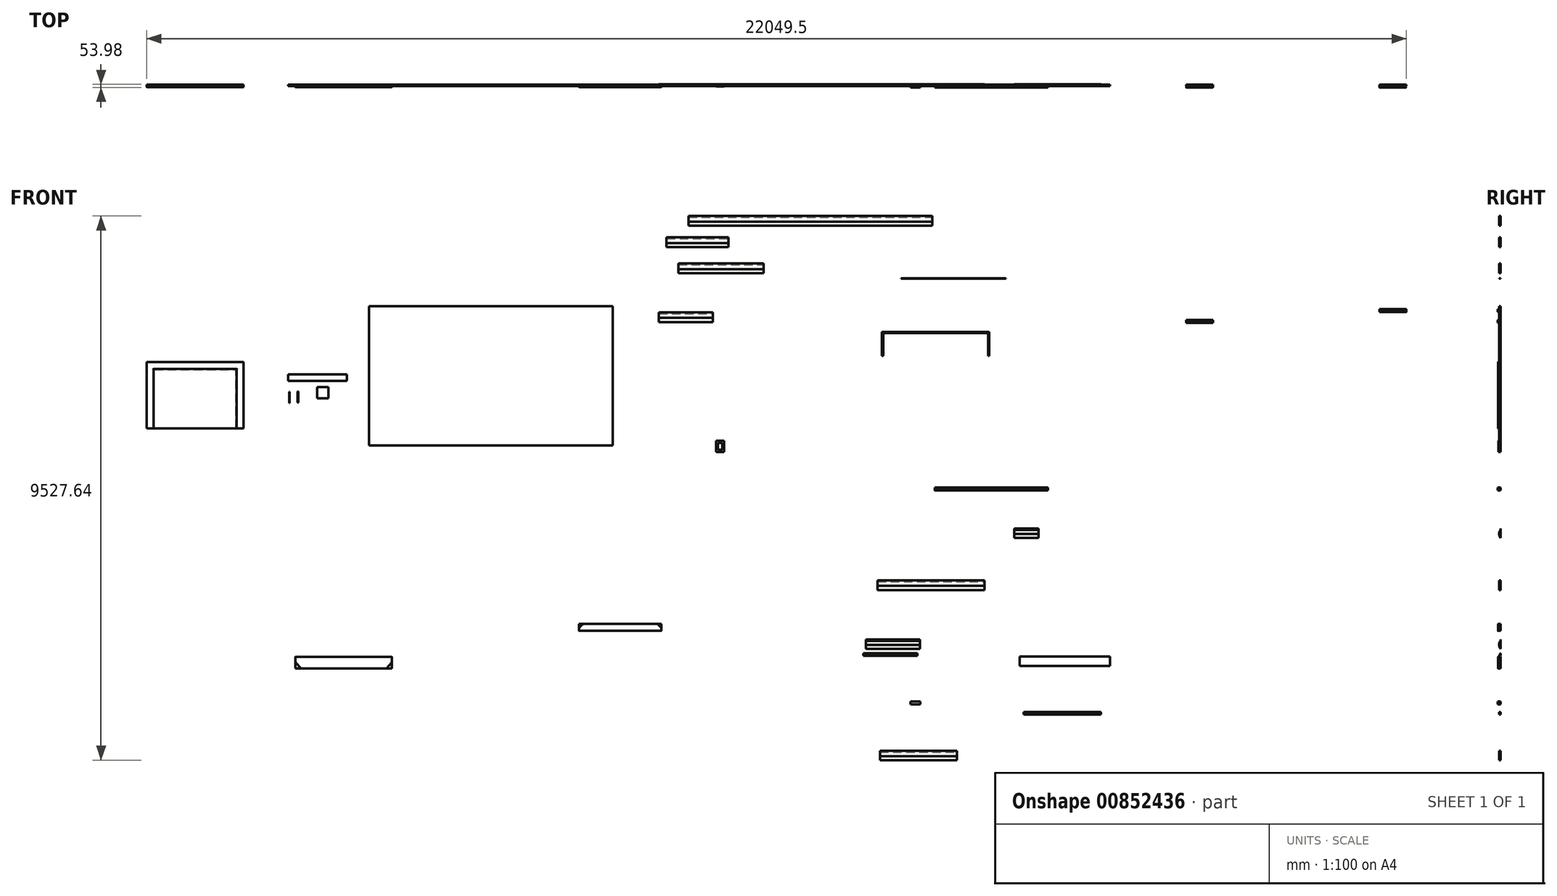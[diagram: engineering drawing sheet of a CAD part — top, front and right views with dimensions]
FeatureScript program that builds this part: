
annotation { "Feature Type Name" : "Feature", "Feature Type Description" : "" }
export const myFeature = defineFeature(function(context is Context, id is Id, definition is map)
    precondition{}
    {
        {
            var Q0;
            Q0=qCreatedBy(makeId("Front.planeOp"),FACE);
            var sketch = newSketch(context, id + "F0", { "sketchPlane" : qUnion([Q0])});
            skLineSegment(sketch, "E0.bottom", {"start": v(2133.6, -1219.2) * mm, "end": v(-2133.6, -1219.2) * mm});
            skLineSegment(sketch, "E0.top", {"start": v(2133.6, 1219.2) * mm, "end": v(-2133.6, 1219.2) * mm});
            skLineSegment(sketch, "E0.left", {"start": v(2133.6, -1219.2) * mm, "end": v(2133.6, 1219.2) * mm});
            skLineSegment(sketch, "E0.right", {"start": v(-2133.6, -1219.2) * mm, "end": v(-2133.6, 1219.2) * mm});
            skPoint(sketch, "E0.middle", {"position": v(0, 0) * mm});
            skLineSegment(sketch, "E1", {"start": v(1047.75, -1219.2) * mm, "end": v(1047.75, 274.79) * mm, "construction": true});
            skLineSegment(sketch, "E2", {"start": v(-644.53, -1219.2) * mm, "end": v(-644.53, 378.54) * mm, "construction": true});
            skLineSegment(sketch, "E3", {"start": v(-966.88, 254) * mm, "end": v(1301.85, 254) * mm, "construction": true});
            skLineSegment(sketch, "E4.bottom", {"start": v(3460.45, 2798.97) * mm, "end": v(7727.65, 2798.97) * mm});
            skLineSegment(sketch, "E4.top", {"start": v(3460.45, 2627.52) * mm, "end": v(7727.65, 2627.52) * mm});
            skLineSegment(sketch, "E4.left", {"start": v(3460.45, 2798.97) * mm, "end": v(3460.45, 2627.52) * mm});
            skLineSegment(sketch, "E4.right", {"start": v(7727.65, 2798.97) * mm, "end": v(7727.65, 2627.52) * mm});
            skLineSegment(sketch, "E5", {"start": v(3460.45, 2773.57) * mm, "end": v(7727.65, 2773.57) * mm});
            skLineSegment(sketch, "E6.bottom", {"start": v(4161.2, 2251.66) * mm, "end": v(3075.35, 2251.66) * mm});
            skLineSegment(sketch, "E6.top", {"start": v(4161.2, 2423.11) * mm, "end": v(3075.35, 2423.11) * mm});
            skLineSegment(sketch, "E6.left", {"start": v(4161.2, 2251.66) * mm, "end": v(4161.2, 2423.11) * mm});
            skLineSegment(sketch, "E6.right", {"start": v(3075.35, 2251.66) * mm, "end": v(3075.35, 2423.11) * mm});
            skPoint(sketch, "E6.middle", {"position": v(3618.27, 2337.39) * mm});
            skLineSegment(sketch, "E7.bottom", {"start": v(4772.4, 1795.08) * mm, "end": v(3283.32, 1795.08) * mm});
            skLineSegment(sketch, "E7.top", {"start": v(4772.4, 1966.53) * mm, "end": v(3283.32, 1966.53) * mm});
            skLineSegment(sketch, "E7.left", {"start": v(4772.4, 1795.08) * mm, "end": v(4772.4, 1966.53) * mm});
            skLineSegment(sketch, "E7.right", {"start": v(3283.32, 1795.08) * mm, "end": v(3283.32, 1966.53) * mm});
            skPoint(sketch, "E7.middle", {"position": v(4027.86, 1880.8) * mm});
            skLineSegment(sketch, "E8", {"start": v(3075.35, 2397.71) * mm, "end": v(4161.2, 2397.71) * mm});
            skLineSegment(sketch, "E9", {"start": v(3283.32, 1941.13) * mm, "end": v(4772.4, 1941.13) * mm});
            skLineSegment(sketch, "E10.bottom", {"start": v(4082.73, -1332.54) * mm, "end": v(3943.03, -1332.54) * mm});
            skLineSegment(sketch, "E10.top", {"start": v(4082.73, -1135.69) * mm, "end": v(3943.03, -1135.69) * mm});
            skLineSegment(sketch, "E10.left", {"start": v(4082.73, -1332.54) * mm, "end": v(4082.73, -1135.69) * mm});
            skLineSegment(sketch, "E10.right", {"start": v(3943.03, -1332.54) * mm, "end": v(3943.03, -1135.69) * mm});
            skPoint(sketch, "E10.middle", {"position": v(4012.88, -1234.11) * mm});
            skLineSegment(sketch, "E11.bottom", {"start": v(4051.44, -1295.6) * mm, "end": v(3974.33, -1295.6) * mm});
            skLineSegment(sketch, "E11.top", {"start": v(4051.44, -1172.61) * mm, "end": v(3974.33, -1172.61) * mm});
            skLineSegment(sketch, "E11.left", {"start": v(4051.44, -1295.6) * mm, "end": v(4051.44, -1172.61) * mm});
            skLineSegment(sketch, "E11.right", {"start": v(3974.33, -1295.6) * mm, "end": v(3974.33, -1172.61) * mm});
            skLineSegment(sketch, "E12.bottom", {"start": v(3886, 940.69) * mm, "end": v(2939.84, 940.69) * mm});
            skLineSegment(sketch, "E12.top", {"start": v(3886, 1112.14) * mm, "end": v(2939.84, 1112.14) * mm});
            skLineSegment(sketch, "E12.left", {"start": v(3886, 940.69) * mm, "end": v(3886, 1112.14) * mm});
            skLineSegment(sketch, "E12.right", {"start": v(2939.84, 940.69) * mm, "end": v(2939.84, 1112.14) * mm});
            skPoint(sketch, "E12.middle", {"position": v(3412.92, 1026.41) * mm});
            skLineSegment(sketch, "E13", {"start": v(2939.84, 1086.74) * mm, "end": v(3886, 1086.74) * mm});
            skLineSegment(sketch, "E14.bottom", {"start": v(-1731.12, -5127.06) * mm, "end": v(-3423.4, -5127.06) * mm});
            skLineSegment(sketch, "E14.top", {"start": v(-1731.12, -4923.86) * mm, "end": v(-3423.4, -4923.86) * mm});
            skLineSegment(sketch, "E14.left", {"start": v(-1731.12, -5127.06) * mm, "end": v(-1731.12, -4923.86) * mm});
            skLineSegment(sketch, "E14.right", {"start": v(-3423.4, -5127.06) * mm, "end": v(-3423.4, -4923.86) * mm});
            skPoint(sketch, "E14.middle", {"position": v(-2577.25, -5025.46) * mm});
            skLineSegment(sketch, "E15", {"start": v(-3423.4, -5012.76) * mm, "end": v(-3321.8, -5127.06) * mm});
            skLineSegment(sketch, "E16", {"start": v(-1832.72, -5127.06) * mm, "end": v(-1731.12, -5012.76) * mm});
            skLineSegment(sketch, "E17.bottom", {"start": v(2982.98, -4465.71) * mm, "end": v(1544.7, -4465.71) * mm});
            skLineSegment(sketch, "E17.top", {"start": v(2982.98, -4345.06) * mm, "end": v(1544.7, -4345.06) * mm});
            skLineSegment(sketch, "E17.left", {"start": v(2982.98, -4465.71) * mm, "end": v(2982.98, -4345.06) * mm});
            skLineSegment(sketch, "E17.right", {"start": v(1544.7, -4465.71) * mm, "end": v(1544.7, -4345.06) * mm});
            skPoint(sketch, "E17.middle", {"position": v(2263.85, -4405.39) * mm});
            skLineSegment(sketch, "E18.bottom", {"start": v(-4331.9, -920.82) * mm, "end": v(-6024.17, -920.82) * mm});
            skLineSegment(sketch, "E18.top", {"start": v(-4331.9, 238.05) * mm, "end": v(-6024.17, 238.05) * mm});
            skLineSegment(sketch, "E18.left", {"start": v(-4331.9, -920.82) * mm, "end": v(-4331.9, 238.05) * mm});
            skLineSegment(sketch, "E18.right", {"start": v(-6024.17, -920.82) * mm, "end": v(-6024.17, 238.05) * mm});
            skLineSegment(sketch, "E19.bottom", {"start": v(-4452.55, -920.82) * mm, "end": v(-5903.52, -920.82) * mm});
            skLineSegment(sketch, "E19.top", {"start": v(-4452.55, 117.4) * mm, "end": v(-5903.52, 117.4) * mm});
            skLineSegment(sketch, "E19.left", {"start": v(-4452.55, -920.82) * mm, "end": v(-4452.55, 117.4) * mm});
            skLineSegment(sketch, "E19.right", {"start": v(-5903.52, -920.82) * mm, "end": v(-5903.52, 117.4) * mm});
            skLineSegment(sketch, "E20.bottom", {"start": v(-5890.82, -920.82) * mm, "end": v(-4465.25, -920.82) * mm});
            skLineSegment(sketch, "E20.top", {"start": v(-5890.82, 107.88) * mm, "end": v(-4465.25, 107.88) * mm});
            skLineSegment(sketch, "E20.left", {"start": v(-5890.82, -920.82) * mm, "end": v(-5890.82, 107.88) * mm});
            skLineSegment(sketch, "E20.right", {"start": v(-4465.25, -920.82) * mm, "end": v(-4465.25, 107.88) * mm});
            skLineSegment(sketch, "E21.bottom", {"start": v(-3522.66, -473.47) * mm, "end": v(-3530.6, -473.47) * mm});
            skLineSegment(sketch, "E21.top", {"start": v(-3522.66, -276.62) * mm, "end": v(-3530.6, -276.62) * mm});
            skLineSegment(sketch, "E21.left", {"start": v(-3522.66, -473.47) * mm, "end": v(-3522.66, -276.62) * mm});
            skLineSegment(sketch, "E21.right", {"start": v(-3530.6, -473.47) * mm, "end": v(-3530.6, -276.62) * mm});
            skPoint(sketch, "E21.middle", {"position": v(-3526.63, -375.05) * mm});
            skLineSegment(sketch, "E22.bottom", {"start": v(-2844.05, -391.52) * mm, "end": v(-3040.9, -391.52) * mm});
            skLineSegment(sketch, "E22.top", {"start": v(-2844.05, -194.67) * mm, "end": v(-3040.9, -194.67) * mm});
            skLineSegment(sketch, "E22.left", {"start": v(-2844.05, -391.52) * mm, "end": v(-2844.05, -194.67) * mm});
            skLineSegment(sketch, "E22.right", {"start": v(-3040.9, -391.52) * mm, "end": v(-3040.9, -194.67) * mm});
            skPoint(sketch, "E22.middle", {"position": v(-2942.48, -293.1) * mm});
            skLineSegment(sketch, "E23.bottom", {"start": v(-3373.18, -472.42) * mm, "end": v(-3385.88, -472.42) * mm});
            skLineSegment(sketch, "E23.top", {"start": v(-3373.18, -275.57) * mm, "end": v(-3385.88, -275.57) * mm});
            skLineSegment(sketch, "E23.left", {"start": v(-3373.18, -472.42) * mm, "end": v(-3373.18, -275.57) * mm});
            skLineSegment(sketch, "E23.right", {"start": v(-3385.88, -472.42) * mm, "end": v(-3385.88, -275.57) * mm});
            skPoint(sketch, "E23.middle", {"position": v(-3379.53, -374) * mm});
            skLineSegment(sketch, "E24.bottom", {"start": v(9756.5, -2005.6) * mm, "end": v(7775.3, -2005.6) * mm});
            skLineSegment(sketch, "E24.top", {"start": v(9756.5, -1954.8) * mm, "end": v(7775.3, -1954.8) * mm});
            skLineSegment(sketch, "E24.left", {"start": v(9756.5, -2005.6) * mm, "end": v(9756.5, -1954.8) * mm});
            skLineSegment(sketch, "E24.right", {"start": v(7775.3, -2005.6) * mm, "end": v(7775.3, -1954.8) * mm});
            skPoint(sketch, "E24.middle", {"position": v(8765.9, -1980.2) * mm});
            skLineSegment(sketch, "E25.bottom", {"start": v(12640.94, 979.02) * mm, "end": v(12171.04, 979.02) * mm});
            skLineSegment(sketch, "E25.top", {"start": v(12640.94, 928.22) * mm, "end": v(12171.04, 928.22) * mm});
            skLineSegment(sketch, "E25.left", {"start": v(12640.94, 979.02) * mm, "end": v(12640.94, 928.22) * mm});
            skLineSegment(sketch, "E25.right", {"start": v(12171.04, 979.02) * mm, "end": v(12171.04, 928.22) * mm});
            skPoint(sketch, "E25.middle", {"position": v(12405.99, 953.62) * mm});
            skLineSegment(sketch, "E26.bottom", {"start": v(16025.35, 1169.27) * mm, "end": v(15555.45, 1169.27) * mm});
            skLineSegment(sketch, "E26.top", {"start": v(16025.35, 1118.47) * mm, "end": v(15555.45, 1118.47) * mm});
            skLineSegment(sketch, "E26.left", {"start": v(16025.35, 1169.27) * mm, "end": v(16025.35, 1118.47) * mm});
            skLineSegment(sketch, "E26.right", {"start": v(15555.45, 1169.27) * mm, "end": v(15555.45, 1118.47) * mm});
            skPoint(sketch, "E26.middle", {"position": v(15790.4, 1143.87) * mm});
            skLineSegment(sketch, "E27.bottom", {"start": v(8727.97, 351.1) * mm, "end": v(8705.74, 351.1) * mm});
            skLineSegment(sketch, "E27.top", {"start": v(8727.97, 770.2) * mm, "end": v(6848.37, 770.2) * mm});
            skLineSegment(sketch, "E27.left", {"start": v(8727.97, 351.1) * mm, "end": v(8727.97, 770.2) * mm});
            skLineSegment(sketch, "E27.right", {"start": v(6848.37, 351.1) * mm, "end": v(6848.37, 770.2) * mm});
            skPoint(sketch, "E27.middle", {"position": v(7788.17, 560.64) * mm});
            skLineSegment(sketch, "E28.top", {"start": v(6870.6, 751.46) * mm, "end": v(8705.74, 751.46) * mm});
            skLineSegment(sketch, "E28.left", {"start": v(6870.6, 351.1) * mm, "end": v(6870.6, 751.46) * mm});
            skLineSegment(sketch, "E28.right", {"start": v(8705.74, 351.1) * mm, "end": v(8705.74, 751.46) * mm});
            skLineSegment(sketch, "E29.trimOffspring", {"start": v(6870.6, 351.1) * mm, "end": v(6848.37, 351.1) * mm});
            skLineSegment(sketch, "E30.bottom", {"start": v(-2520.18, -86.53) * mm, "end": v(-3552.06, -86.53) * mm});
            skLineSegment(sketch, "E30.top", {"start": v(-2520.18, 27.77) * mm, "end": v(-3552.06, 27.77) * mm});
            skLineSegment(sketch, "E30.left", {"start": v(-2520.18, -86.53) * mm, "end": v(-2520.18, 27.77) * mm});
            skLineSegment(sketch, "E30.right", {"start": v(-3552.06, -86.53) * mm, "end": v(-3552.06, 27.77) * mm});
            skPoint(sketch, "E30.middle", {"position": v(-3036.12, -29.38) * mm});
            skLineSegment(sketch, "E31.bottom", {"start": v(9016.83, 1702.28) * mm, "end": v(7181.68, 1702.28) * mm});
            skLineSegment(sketch, "E31.top", {"start": v(9016.83, 1710.22) * mm, "end": v(7181.68, 1710.22) * mm});
            skLineSegment(sketch, "E31.left", {"start": v(9016.83, 1702.28) * mm, "end": v(9016.83, 1710.22) * mm});
            skLineSegment(sketch, "E31.right", {"start": v(7181.68, 1702.28) * mm, "end": v(7181.68, 1710.22) * mm});
            skPoint(sketch, "E31.middle", {"position": v(8099.26, 1706.25) * mm});
            skLineSegment(sketch, "E32.bottom", {"start": v(6770.2, -3752.52) * mm, "end": v(8639.64, -3752.52) * mm});
            skLineSegment(sketch, "E32.top", {"start": v(6770.2, -3581.07) * mm, "end": v(8639.64, -3581.07) * mm});
            skLineSegment(sketch, "E32.left", {"start": v(6770.2, -3752.52) * mm, "end": v(6770.2, -3581.07) * mm});
            skLineSegment(sketch, "E32.right", {"start": v(8639.64, -3752.52) * mm, "end": v(8639.64, -3581.07) * mm});
            skLineSegment(sketch, "E33.bottom", {"start": v(7344.23, -5752.08) * mm, "end": v(7515.68, -5752.08) * mm});
            skLineSegment(sketch, "E33.top", {"start": v(7344.23, -5701.28) * mm, "end": v(7515.68, -5701.28) * mm});
            skLineSegment(sketch, "E33.left", {"start": v(7344.23, -5752.08) * mm, "end": v(7344.23, -5701.28) * mm});
            skLineSegment(sketch, "E33.right", {"start": v(7515.68, -5752.08) * mm, "end": v(7515.68, -5701.28) * mm});
            skLineSegment(sketch, "E34.bottom", {"start": v(6811, -6728.67) * mm, "end": v(8160.37, -6728.67) * mm});
            skLineSegment(sketch, "E34.top", {"start": v(6811, -6563.57) * mm, "end": v(8160.37, -6563.57) * mm});
            skLineSegment(sketch, "E34.left", {"start": v(6811, -6728.67) * mm, "end": v(6811, -6563.57) * mm});
            skLineSegment(sketch, "E34.right", {"start": v(8160.37, -6728.67) * mm, "end": v(8160.37, -6563.57) * mm});
            skLineSegment(sketch, "E35", {"start": v(6770.2, -3606.47) * mm, "end": v(8639.64, -3606.47) * mm});
            skLineSegment(sketch, "E36", {"start": v(6811, -6588.97) * mm, "end": v(8160.37, -6588.97) * mm});
            skLineSegment(sketch, "E37.bottom", {"start": v(6564.1, -4778.8) * mm, "end": v(7510.25, -4778.8) * mm});
            skLineSegment(sketch, "E37.top", {"start": v(6564.1, -4613.7) * mm, "end": v(7510.25, -4613.7) * mm});
            skLineSegment(sketch, "E37.left", {"start": v(6564.1, -4778.8) * mm, "end": v(6564.1, -4613.7) * mm});
            skLineSegment(sketch, "E37.right", {"start": v(7510.25, -4778.8) * mm, "end": v(7510.25, -4613.7) * mm});
            skLineSegment(sketch, "E38.bottom", {"start": v(9256.06, -5080.82) * mm, "end": v(10837.31, -5080.82) * mm});
            skLineSegment(sketch, "E38.top", {"start": v(9256.06, -4915.72) * mm, "end": v(10837.31, -4915.72) * mm});
            skLineSegment(sketch, "E38.left", {"start": v(9256.06, -5080.82) * mm, "end": v(9256.06, -4915.72) * mm});
            skLineSegment(sketch, "E38.right", {"start": v(10837.31, -5080.82) * mm, "end": v(10837.31, -4915.72) * mm});
            skLineSegment(sketch, "E39.bottom", {"start": v(9329.57, -5932.4) * mm, "end": v(10678.95, -5932.4) * mm});
            skLineSegment(sketch, "E39.top", {"start": v(9329.57, -5887.95) * mm, "end": v(10678.95, -5887.95) * mm});
            skLineSegment(sketch, "E39.left", {"start": v(9329.57, -5932.4) * mm, "end": v(9329.57, -5887.95) * mm});
            skLineSegment(sketch, "E39.right", {"start": v(10678.95, -5932.4) * mm, "end": v(10678.95, -5887.95) * mm});
            skLineSegment(sketch, "E40", {"start": v(6564.1, -4639.1) * mm, "end": v(7510.25, -4639.1) * mm});
            skLineSegment(sketch, "E41.bottom", {"start": v(6523.58, -4857.86) * mm, "end": v(7469.73, -4857.86) * mm});
            skLineSegment(sketch, "E41.top", {"start": v(6523.58, -4902.3) * mm, "end": v(7469.73, -4902.3) * mm});
            skLineSegment(sketch, "E41.left", {"start": v(6523.58, -4857.86) * mm, "end": v(6523.58, -4902.3) * mm});
            skLineSegment(sketch, "E41.right", {"start": v(7469.73, -4857.86) * mm, "end": v(7469.73, -4902.3) * mm});
            skLineSegment(sketch, "E42.bottom", {"start": v(9586.54, -2837.34) * mm, "end": v(9161.1, -2837.34) * mm});
            skLineSegment(sketch, "E42.top", {"start": v(9586.54, -2672.24) * mm, "end": v(9161.1, -2672.24) * mm});
            skLineSegment(sketch, "E42.left", {"start": v(9586.54, -2837.34) * mm, "end": v(9586.54, -2672.24) * mm});
            skLineSegment(sketch, "E42.right", {"start": v(9161.1, -2837.34) * mm, "end": v(9161.1, -2672.24) * mm});
            skPoint(sketch, "E42.middle", {"position": v(9373.82, -2754.79) * mm});
            skLineSegment(sketch, "E43", {"start": v(9161.1, -2697.64) * mm, "end": v(9586.54, -2697.64) * mm});
            skSolve(sketch);
        }
        {
            var Q0;
            {var subQ0=sQuery(id+"F0.wireOp",EDGE,"E7.bottom");Q0=makeQuery(id+"F0.imprint","IMPRINT",FACE,{"disambiguationData":[TD([[makeQuery(id+"F0.imprint","IMPRINT",EDGE,{"derivedFrom":subQ0}),-1.0]])]});}
            var Q1;
            {var subQ0=sQuery(id+"F0.wireOp",EDGE,"E4.top");Q1=makeQuery(id+"F0.imprint","IMPRINT",FACE,{"disambiguationData":[TD([[makeQuery(id+"F0.imprint","IMPRINT",EDGE,{"derivedFrom":subQ0}),1.0]])]});}
            var Q2;
            {var subQ0=sQuery(id+"F0.wireOp",EDGE,"E6.bottom");Q2=makeQuery(id+"F0.imprint","IMPRINT",FACE,{"disambiguationData":[TD([[makeQuery(id+"F0.imprint","IMPRINT",EDGE,{"derivedFrom":subQ0}),-1.0]])]});}
            var Q3;
            {var subQ0=sQuery(id+"F0.wireOp",EDGE,"E12.bottom");Q3=makeQuery(id+"F0.imprint","IMPRINT",FACE,{"disambiguationData":[TD([[makeQuery(id+"F0.imprint","IMPRINT",EDGE,{"derivedFrom":subQ0}),-1.0]])]});}
            extrude(context, id + "F1", {"entities" : qUnion([Q0, Q1, Q2, Q3]), "depth" : 25.4 * mm, "offsetDistance" : 25.4 * mm});
        }
        {
            var Q0;
            Q0=makeQuery(id+"F1.opExtrude","CAP_EDGE",EDGE,{"disambiguationData":[OSD([sQuery(id+"F0.wireOp",EDGE,"E4.top")])],"isStart":false});
            var Q1;
            Q1=makeQuery(id+"F1.opExtrude","CAP_EDGE",EDGE,{"disambiguationData":[OSD([sQuery(id+"F0.wireOp",EDGE,"E5")])],"isStart":false});
            var Q2;
            Q2=makeQuery(id+"F1.opExtrude","CAP_EDGE",EDGE,{"disambiguationData":[OSD([sQuery(id+"F0.wireOp",EDGE,"E6.bottom")])],"isStart":false});
            var Q3;
            Q3=makeQuery(id+"F1.opExtrude","CAP_EDGE",EDGE,{"disambiguationData":[OSD([sQuery(id+"F0.wireOp",EDGE,"E8")])],"isStart":false});
            var Q4;
            Q4=makeQuery(id+"F1.opExtrude","CAP_EDGE",EDGE,{"disambiguationData":[OSD([sQuery(id+"F0.wireOp",EDGE,"E9")])],"isStart":false});
            var Q5;
            Q5=makeQuery(id+"F1.opExtrude","CAP_EDGE",EDGE,{"disambiguationData":[OSD([sQuery(id+"F0.wireOp",EDGE,"E7.bottom")])],"isStart":false});
            var Q6;
            Q6=makeQuery(id+"F1.opExtrude","CAP_EDGE",EDGE,{"disambiguationData":[OSD([sQuery(id+"F0.wireOp",EDGE,"E13")])],"isStart":false});
            var Q7;
            Q7=makeQuery(id+"F1.opExtrude","CAP_EDGE",EDGE,{"disambiguationData":[OSD([sQuery(id+"F0.wireOp",EDGE,"E12.bottom")])],"isStart":false});
            fillet(context, id + "F2", {"entities" : qUnion([Q0, Q1, Q2, Q3, Q4, Q5, Q6, Q7]), "radius" : 127 * mm, "tangentPropagation" : true, "allowEdgeOverflow" : false});
        }
        {
            var Q0;
            {var subQ0=sQuery(id+"F0.wireOp",EDGE,"E6.bottom");Q0=makeQuery(id+"F0.imprint","IMPRINT",FACE,{"disambiguationData":[TD([[makeQuery(id+"F0.imprint","IMPRINT",EDGE,{"derivedFrom":subQ0}),-1.0]])]});}
            var Q1;
            {var subQ0=sQuery(id+"F0.wireOp",EDGE,"E6.top");Q1=makeQuery(id+"F0.imprint","IMPRINT",FACE,{"disambiguationData":[TD([[makeQuery(id+"F0.imprint","IMPRINT",EDGE,{"derivedFrom":subQ0}),1.0]])]});}
            extrude(context, id + "F3", {"entities" : qUnion([Q0, Q1]), "operationType" : NewBodyOperationType.ADD, "oppositeDirection" : true, "depth" : 3.17 * mm, "offsetDistance" : 25.4 * mm});
        }
        {
            var Q0;
            {var subQ0=sQuery(id+"F0.wireOp",EDGE,"E7.top");Q0=makeQuery(id+"F0.imprint","IMPRINT",FACE,{"disambiguationData":[TD([[makeQuery(id+"F0.imprint","IMPRINT",EDGE,{"derivedFrom":subQ0}),1.0]])]});}
            var Q1;
            {var subQ0=sQuery(id+"F0.wireOp",EDGE,"E7.bottom");Q1=makeQuery(id+"F0.imprint","IMPRINT",FACE,{"disambiguationData":[TD([[makeQuery(id+"F0.imprint","IMPRINT",EDGE,{"derivedFrom":subQ0}),-1.0]])]});}
            extrude(context, id + "F4", {"entities" : qUnion([Q0, Q1]), "operationType" : NewBodyOperationType.ADD, "oppositeDirection" : true, "depth" : 3.17 * mm, "offsetDistance" : 25.4 * mm});
        }
        {
            var Q0;
            {var subQ0=sQuery(id+"F0.wireOp",EDGE,"E4.top");Q0=makeQuery(id+"F0.imprint","IMPRINT",FACE,{"disambiguationData":[TD([[makeQuery(id+"F0.imprint","IMPRINT",EDGE,{"derivedFrom":subQ0}),1.0]])]});}
            var Q1;
            {var subQ0=sQuery(id+"F0.wireOp",EDGE,"E4.bottom");Q1=makeQuery(id+"F0.imprint","IMPRINT",FACE,{"disambiguationData":[TD([[makeQuery(id+"F0.imprint","IMPRINT",EDGE,{"derivedFrom":subQ0}),-1.0]])]});}
            extrude(context, id + "F5", {"entities" : qUnion([Q0, Q1]), "operationType" : NewBodyOperationType.ADD, "oppositeDirection" : true, "depth" : 3.17 * mm, "offsetDistance" : 25.4 * mm});
        }
        {
            var Q0;
            Q0=makeQuery(id+"F0.imprint","IMPRINT",FACE,{"disambiguationData":[TD([[makeQuery(id+"F0.imprint","IMPRINT",EDGE,{"derivedFrom":sQuery(id+"F0.wireOp",EDGE,"E10.bottom")}),-1.0]])]});
            extrude(context, id + "F6", {"entities" : qUnion([Q0]), "depth" : 34.92 * mm, "offsetDistance" : 25.4 * mm});
        }
        {
            var Q0;
            {var subQ0=sQuery(id+"F0.wireOp",EDGE,"E12.bottom");Q0=makeQuery(id+"F0.imprint","IMPRINT",FACE,{"disambiguationData":[TD([[makeQuery(id+"F0.imprint","IMPRINT",EDGE,{"derivedFrom":subQ0}),-1.0]])]});}
            var Q1;
            {var subQ0=sQuery(id+"F0.wireOp",EDGE,"E12.top");Q1=makeQuery(id+"F0.imprint","IMPRINT",FACE,{"disambiguationData":[TD([[makeQuery(id+"F0.imprint","IMPRINT",EDGE,{"derivedFrom":subQ0}),1.0]])]});}
            extrude(context, id + "F7", {"entities" : qUnion([Q0, Q1]), "operationType" : NewBodyOperationType.ADD, "oppositeDirection" : true, "depth" : 3.17 * mm, "offsetDistance" : 25.4 * mm});
        }
        {
            var Q0;
            {var subQ1=sQuery(id+"F0.wireOp",EDGE,"E14.top");Q0=makeQuery(id+"F0.imprint","IMPRINT",FACE,{"disambiguationData":[TD([[makeQuery(id+"F0.imprint","IMPRINT",EDGE,{"derivedFrom":subQ1}),1.0]])]});}
            extrude(context, id + "F8", {"entities" : qUnion([Q0]), "depth" : 44.45 * mm, "offsetDistance" : 25.4 * mm});
        }
        {
            var Q0;
            Q0=makeQuery(id+"F8.opExtrude","CAP_EDGE",EDGE,{"disambiguationData":[OSD([sQuery(id+"F0.wireOp",EDGE,"E14.bottom")])],"isStart":false});
            var Q1;
            Q1=makeQuery(id+"F8.opExtrude","CAP_EDGE",EDGE,{"disambiguationData":[OSD([sQuery(id+"F0.wireOp",EDGE,"E15")])],"isStart":false});
            var Q2;
            Q2=makeQuery(id+"F8.opExtrude","CAP_EDGE",EDGE,{"disambiguationData":[OSD([sQuery(id+"F0.wireOp",EDGE,"E14.right")])],"isStart":false});
            var Q3;
            Q3=makeQuery(id+"F8.opExtrude","CAP_EDGE",EDGE,{"disambiguationData":[OSD([sQuery(id+"F0.wireOp",EDGE,"E16")])],"isStart":false});
            chamfer(context, id + "F9", {"entities" : qUnion([Q0, Q1, Q2, Q3]), "width" : 5.08 * mm, "tangentPropagation" : true});
        }
        {
            var Q0;
            Q0=makeQuery(id+"F8.opExtrude","CAP_FACE",FACE,{"disambiguationData":[OSD([sQuery(id+"F0.wireOp",EDGE,"E14.bottom"),sQuery(id+"F0.wireOp",EDGE,"E14.top"),sQuery(id+"F0.wireOp",EDGE,"E14.left"),sQuery(id+"F0.wireOp",EDGE,"E14.right"),sQuery(id+"F0.wireOp",EDGE,"E15"),sQuery(id+"F0.wireOp",EDGE,"E16")])],"isStart":false});
            var Q1;
            Q1=makeQuery(id+"F8.opExtrude","SWEPT_EDGE",EDGE,{"disambiguationData":[OSD([sQuery(id+"F0.wireOp",EDGE,"E14.bottom"),sQuery(id+"F0.wireOp",EDGE,"E16")])]});
            var Q2;
            Q2=makeQuery(id+"F8.opExtrude","CAP_EDGE",EDGE,{"disambiguationData":[OSD([sQuery(id+"F0.wireOp",EDGE,"E14.bottom")])],"isStart":true});
            var Q3;
            Q3=makeQuery(id+"F8.opExtrude","CAP_EDGE",EDGE,{"disambiguationData":[OSD([sQuery(id+"F0.wireOp",EDGE,"E16")])],"isStart":true});
            var Q4;
            Q4=makeQuery(id+"F8.opExtrude","SWEPT_EDGE",EDGE,{"disambiguationData":[OSD([sQuery(id+"F0.wireOp",EDGE,"E14.left"),sQuery(id+"F0.wireOp",EDGE,"E16")])]});
            var Q5;
            Q5=makeQuery(id+"F8.opExtrude","SWEPT_EDGE",EDGE,{"disambiguationData":[OSD([sQuery(id+"F0.wireOp",EDGE,"E14.bottom"),sQuery(id+"F0.wireOp",EDGE,"E15")])]});
            var Q6;
            Q6=makeQuery(id+"F8.opExtrude","CAP_EDGE",EDGE,{"disambiguationData":[OSD([sQuery(id+"F0.wireOp",EDGE,"E15")])],"isStart":true});
            var Q7;
            Q7=makeQuery(id+"F8.opExtrude","SWEPT_EDGE",EDGE,{"disambiguationData":[OSD([sQuery(id+"F0.wireOp",EDGE,"E14.right"),sQuery(id+"F0.wireOp",EDGE,"E15")])]});
            var Q8;
            Q8=makeQuery(id+"F8.opExtrude","CAP_EDGE",EDGE,{"disambiguationData":[OSD([sQuery(id+"F0.wireOp",EDGE,"E14.right")])],"isStart":true});
            var Q9;
            Q9=makeQuery(id+"F8.opExtrude","CAP_EDGE",EDGE,{"disambiguationData":[OSD([sQuery(id+"F0.wireOp",EDGE,"E14.left")])],"isStart":true});
            fillet(context, id + "F10", {"entities" : qUnion([Q0, Q1, Q2, Q3, Q4, Q5, Q6, Q7, Q8, Q9]), "radius" : 6.35 * mm, "tangentPropagation" : true, "allowEdgeOverflow" : false});
        }
        {
            var Q0;
            Q0=makeQuery(id+"F0.imprint","IMPRINT",FACE,{"disambiguationData":[TD([[makeQuery(id+"F0.imprint","IMPRINT",EDGE,{"derivedFrom":sQuery(id+"F0.wireOp",EDGE,"E17.bottom")}),-1.0]])]});
            extrude(context, id + "F11", {"entities" : qUnion([Q0]), "depth" : 44.45 * mm, "offsetDistance" : 25.4 * mm});
        }
        {
            var Q0;
            Q0=makeQuery(id+"F11.opExtrude","SWEPT_EDGE",EDGE,{"disambiguationData":[OSD([sQuery(id+"F0.wireOp",EDGE,"E17.top"),sQuery(id+"F0.wireOp",EDGE,"E17.left")])]});
            var Q1;
            Q1=makeQuery(id+"F11.opExtrude","SWEPT_EDGE",EDGE,{"disambiguationData":[OSD([sQuery(id+"F0.wireOp",EDGE,"E17.top"),sQuery(id+"F0.wireOp",EDGE,"E17.right")])]});
            chamfer(context, id + "F12", {"entities" : qUnion([Q0, Q1]), "width" : 69.85 * mm, "tangentPropagation" : true});
        }
        {
            var Q0;
            Q0=makeQuery(id+"F11.opExtrude","CAP_EDGE",EDGE,{"disambiguationData":[OSD([sQuery(id+"F0.wireOp",EDGE,"E17.top")])],"isStart":false});
            var Q1;
            {var subQ0=sQuery(id+"F0.wireOp",EDGE,"E17.right");var subQ1=sQuery(id+"F0.wireOp",EDGE,"E17.top");Q1=makeQuery(id+"F12.opChamfer","BLEND_EDGE",EDGE,{"blendedFrom":[makeQuery(id+"F11.opExtrude","SWEPT_EDGE",EDGE,{"disambiguationData":[OSD([subQ1,subQ0])]}),makeQuery(id+"F11.opExtrude","CAP_FACE",FACE,{"disambiguationData":[OSD([sQuery(id+"F0.wireOp",EDGE,"E17.bottom"),subQ1,sQuery(id+"F0.wireOp",EDGE,"E17.left"),subQ0])],"isStart":false})],"blendedInto":[makeQuery(id+"F11.opExtrude","CAP_FACE",FACE,{"disambiguationData":[OSD([sQuery(id+"F0.wireOp",EDGE,"E17.bottom"),subQ1,sQuery(id+"F0.wireOp",EDGE,"E17.left"),subQ0])],"isStart":false})]});}
            var Q2;
            Q2=makeQuery(id+"F11.opExtrude","CAP_EDGE",EDGE,{"disambiguationData":[OSD([sQuery(id+"F0.wireOp",EDGE,"E17.right")])],"isStart":false});
            var Q3;
            {var subQ0=sQuery(id+"F0.wireOp",EDGE,"E17.left");var subQ1=sQuery(id+"F0.wireOp",EDGE,"E17.top");Q3=makeQuery(id+"F12.opChamfer","BLEND_EDGE",EDGE,{"blendedFrom":[makeQuery(id+"F11.opExtrude","SWEPT_EDGE",EDGE,{"disambiguationData":[OSD([subQ1,subQ0])]}),makeQuery(id+"F11.opExtrude","CAP_FACE",FACE,{"disambiguationData":[OSD([sQuery(id+"F0.wireOp",EDGE,"E17.bottom"),subQ1,subQ0,sQuery(id+"F0.wireOp",EDGE,"E17.right")])],"isStart":false})],"blendedInto":[makeQuery(id+"F11.opExtrude","CAP_FACE",FACE,{"disambiguationData":[OSD([sQuery(id+"F0.wireOp",EDGE,"E17.bottom"),subQ1,subQ0,sQuery(id+"F0.wireOp",EDGE,"E17.right")])],"isStart":false})]});}
            var Q4;
            Q4=makeQuery(id+"F11.opExtrude","CAP_EDGE",EDGE,{"disambiguationData":[OSD([sQuery(id+"F0.wireOp",EDGE,"E17.left")])],"isStart":false});
            chamfer(context, id + "F13", {"entities" : qUnion([Q0, Q1, Q2, Q3, Q4]), "width" : 6.35 * mm, "tangentPropagation" : true});
        }
        {
            var Q0;
            {var subQ0=sQuery(id+"F0.wireOp",EDGE,"E17.right");Q0=makeQuery(id+"F12.opChamfer","BLEND_EDGE",EDGE,{"blendedFrom":[makeQuery(id+"F11.opExtrude","SWEPT_EDGE",EDGE,{"disambiguationData":[OSD([sQuery(id+"F0.wireOp",EDGE,"E17.top"),subQ0])]}),makeQuery(id+"F11.opExtrude","SWEPT_FACE",FACE,{"disambiguationData":[OSD([subQ0])]})],"blendedInto":[makeQuery(id+"F11.opExtrude","SWEPT_FACE",FACE,{"disambiguationData":[OSD([subQ0])]})]});}
            var Q1;
            {var subQ0=sQuery(id+"F0.wireOp",EDGE,"E17.top");Q1=makeQuery(id+"F12.opChamfer","BLEND_EDGE",EDGE,{"blendedFrom":[makeQuery(id+"F11.opExtrude","SWEPT_EDGE",EDGE,{"disambiguationData":[OSD([subQ0,sQuery(id+"F0.wireOp",EDGE,"E17.right")])]}),makeQuery(id+"F11.opExtrude","SWEPT_FACE",FACE,{"disambiguationData":[OSD([subQ0])]})],"blendedInto":[makeQuery(id+"F11.opExtrude","SWEPT_FACE",FACE,{"disambiguationData":[OSD([subQ0])]})]});}
            var Q2;
            Q2=makeQuery(id+"F11.opExtrude","CAP_FACE",FACE,{"disambiguationData":[OSD([sQuery(id+"F0.wireOp",EDGE,"E17.bottom"),sQuery(id+"F0.wireOp",EDGE,"E17.top"),sQuery(id+"F0.wireOp",EDGE,"E17.left"),sQuery(id+"F0.wireOp",EDGE,"E17.right")])],"isStart":false});
            var Q3;
            {var subQ0=sQuery(id+"F0.wireOp",EDGE,"E17.top");Q3=makeQuery(id+"F12.opChamfer","BLEND_EDGE",EDGE,{"blendedFrom":[makeQuery(id+"F11.opExtrude","SWEPT_EDGE",EDGE,{"disambiguationData":[OSD([subQ0,sQuery(id+"F0.wireOp",EDGE,"E17.left")])]}),makeQuery(id+"F11.opExtrude","SWEPT_FACE",FACE,{"disambiguationData":[OSD([subQ0])]})],"blendedInto":[makeQuery(id+"F11.opExtrude","SWEPT_FACE",FACE,{"disambiguationData":[OSD([subQ0])]})]});}
            var Q4;
            {var subQ0=sQuery(id+"F0.wireOp",EDGE,"E17.left");Q4=makeQuery(id+"F12.opChamfer","BLEND_EDGE",EDGE,{"blendedFrom":[makeQuery(id+"F11.opExtrude","SWEPT_EDGE",EDGE,{"disambiguationData":[OSD([sQuery(id+"F0.wireOp",EDGE,"E17.top"),subQ0])]}),makeQuery(id+"F11.opExtrude","SWEPT_FACE",FACE,{"disambiguationData":[OSD([subQ0])]})],"blendedInto":[makeQuery(id+"F11.opExtrude","SWEPT_FACE",FACE,{"disambiguationData":[OSD([subQ0])]})]});}
            fillet(context, id + "F14", {"entities" : qUnion([Q0, Q1, Q2, Q3, Q4]), "radius" : 5.08 * mm, "tangentPropagation" : true, "allowEdgeOverflow" : false});
        }
        {
            var Q0;
            Q0=makeQuery(id+"F0.imprint","IMPRINT",FACE,{"disambiguationData":[TD([[makeQuery(id+"F0.imprint","IMPRINT",EDGE,{"derivedFrom":sQuery(id+"F0.wireOp",EDGE,"E18.top")}),1.0]])]});
            extrude(context, id + "F15", {"entities" : qUnion([Q0]), "depth" : 44.45 * mm, "offsetDistance" : 25.4 * mm});
        }
        {
            var Q0;
            Q0=makeQuery(id+"F15.opExtrude","CAP_EDGE",EDGE,{"disambiguationData":[OSD([sQuery(id+"F0.wireOp",EDGE,"E19.right")])],"isStart":false});
            var Q1;
            Q1=makeQuery(id+"F15.opExtrude","CAP_EDGE",EDGE,{"disambiguationData":[OSD([sQuery(id+"F0.wireOp",EDGE,"E19.top")])],"isStart":false});
            var Q2;
            Q2=makeQuery(id+"F15.opExtrude","CAP_EDGE",EDGE,{"disambiguationData":[OSD([sQuery(id+"F0.wireOp",EDGE,"E19.left")])],"isStart":false});
            chamfer(context, id + "F16", {"entities" : qUnion([Q0, Q1, Q2]), "width" : 6.35 * mm, "tangentPropagation" : true});
        }
        {
            var Q0;
            Q0=makeQuery(id+"F15.opExtrude","CAP_FACE",FACE,{"disambiguationData":[OSD([sQuery(id+"F0.wireOp",EDGE,"E18.bottom"),sQuery(id+"F0.wireOp",EDGE,"E18.top"),sQuery(id+"F0.wireOp",EDGE,"E18.left"),sQuery(id+"F0.wireOp",EDGE,"E18.right"),sQuery(id+"F0.wireOp",EDGE,"E19.top"),sQuery(id+"F0.wireOp",EDGE,"E19.left"),sQuery(id+"F0.wireOp",EDGE,"E19.right")])],"isStart":false});
            fillet(context, id + "F17", {"entities" : qUnion([Q0]), "radius" : 6.35 * mm, "tangentPropagation" : true, "allowEdgeOverflow" : false});
        }
        {
            var Q0;
            Q0=makeQuery(id+"F0.imprint","IMPRINT",FACE,{"disambiguationData":[TD([[makeQuery(id+"F0.imprint","IMPRINT",EDGE,{"derivedFrom":sQuery(id+"F0.wireOp",EDGE,"E22.bottom")}),-1.0]])]});
            var Q1;
            Q1=makeQuery(id+"F0.imprint","IMPRINT",FACE,{"disambiguationData":[TD([[makeQuery(id+"F0.imprint","IMPRINT",EDGE,{"derivedFrom":sQuery(id+"F0.wireOp",EDGE,"E21.bottom")}),-1.0]])]});
            extrude(context, id + "F18", {"entities" : qUnion([Q0, Q1]), "operationType" : NewBodyOperationType.ADD, "depth" : 3.17 * mm, "offsetDistance" : 25.4 * mm});
        }
        {
            var Q0;
            Q0=makeQuery(id+"F0.imprint","IMPRINT",FACE,{"disambiguationData":[TD([[makeQuery(id+"F0.imprint","IMPRINT",EDGE,{"derivedFrom":sQuery(id+"F0.wireOp",EDGE,"E19.top")}),1.0]])]});
            extrude(context, id + "F19", {"entities" : qUnion([Q0]), "depth" : 3.17 * mm, "offsetDistance" : 25.4 * mm});
        }
        {
            var Q0;
            Q0=makeQuery(id+"F0.imprint","IMPRINT",FACE,{"disambiguationData":[TD([[makeQuery(id+"F0.imprint","IMPRINT",EDGE,{"derivedFrom":sQuery(id+"F0.wireOp",EDGE,"E23.bottom")}),-1.0]])]});
            extrude(context, id + "F20", {"entities" : qUnion([Q0]), "depth" : 3.17 * mm, "offsetDistance" : 25.4 * mm});
        }
        {
            var Q0;
            Q0=makeQuery(id+"F0.imprint","IMPRINT",FACE,{"disambiguationData":[TD([[makeQuery(id+"F0.imprint","IMPRINT",EDGE,{"derivedFrom":sQuery(id+"F0.wireOp",EDGE,"E24.bottom")}),-1.0]])]});
            var Q1;
            Q1=makeQuery(id+"F0.imprint","IMPRINT",FACE,{"disambiguationData":[TD([[makeQuery(id+"F0.imprint","IMPRINT",EDGE,{"derivedFrom":sQuery(id+"F0.wireOp",EDGE,"E25.bottom")}),1.0]])]});
            var Q2;
            Q2=makeQuery(id+"F0.imprint","IMPRINT",FACE,{"disambiguationData":[TD([[makeQuery(id+"F0.imprint","IMPRINT",EDGE,{"derivedFrom":sQuery(id+"F0.wireOp",EDGE,"E26.bottom")}),1.0]])]});
            extrude(context, id + "F21", {"entities" : qUnion([Q0, Q1, Q2]), "depth" : 50.8 * mm, "offsetDistance" : 25.4 * mm});
        }
        {
            var Q0;
            Q0=makeQuery(id+"F21.opExtrude","CAP_EDGE",EDGE,{"disambiguationData":[OSD([sQuery(id+"F0.wireOp",EDGE,"E26.bottom")])],"isStart":false});
            var Q1;
            Q1=makeQuery(id+"F21.opExtrude","CAP_EDGE",EDGE,{"disambiguationData":[OSD([sQuery(id+"F0.wireOp",EDGE,"E26.top")])],"isStart":false});
            var Q2;
            Q2=makeQuery(id+"F21.opExtrude","CAP_EDGE",EDGE,{"disambiguationData":[OSD([sQuery(id+"F0.wireOp",EDGE,"E25.bottom")])],"isStart":false});
            var Q3;
            Q3=makeQuery(id+"F21.opExtrude","CAP_EDGE",EDGE,{"disambiguationData":[OSD([sQuery(id+"F0.wireOp",EDGE,"E25.top")])],"isStart":false});
            var Q4;
            Q4=makeQuery(id+"F21.opExtrude","CAP_EDGE",EDGE,{"disambiguationData":[OSD([sQuery(id+"F0.wireOp",EDGE,"E24.top")])],"isStart":false});
            var Q5;
            Q5=makeQuery(id+"F21.opExtrude","CAP_EDGE",EDGE,{"disambiguationData":[OSD([sQuery(id+"F0.wireOp",EDGE,"E24.bottom")])],"isStart":false});
            chamfer(context, id + "F22", {"entities" : qUnion([Q0, Q1, Q2, Q3, Q4, Q5]), "width" : 5.08 * mm, "tangentPropagation" : true});
        }
        {
            var Q0;
            Q0=makeQuery(id+"F21.opExtrude","CAP_EDGE",EDGE,{"disambiguationData":[OSD([sQuery(id+"F0.wireOp",EDGE,"E24.left")])],"isStart":true});
            var Q1;
            Q1=makeQuery(id+"F21.opExtrude","CAP_EDGE",EDGE,{"disambiguationData":[OSD([sQuery(id+"F0.wireOp",EDGE,"E24.right")])],"isStart":true});
            var Q2;
            Q2=makeQuery(id+"F21.opExtrude","CAP_EDGE",EDGE,{"disambiguationData":[OSD([sQuery(id+"F0.wireOp",EDGE,"E25.right")])],"isStart":true});
            var Q3;
            Q3=makeQuery(id+"F21.opExtrude","CAP_EDGE",EDGE,{"disambiguationData":[OSD([sQuery(id+"F0.wireOp",EDGE,"E26.left")])],"isStart":true});
            chamfer(context, id + "F23", {"entities" : qUnion([Q0, Q1, Q2, Q3]), "width" : 50.8 * mm, "tangentPropagation" : true});
        }
        {
            var Q0;
            {var subQ0=sQuery(id+"F0.wireOp",EDGE,"E26.bottom");Q0=makeQuery(id+"F22.opChamfer","BLEND_EDGE",EDGE,{"blendedFrom":[makeQuery(id+"F21.opExtrude","CAP_EDGE",EDGE,{"disambiguationData":[OSD([subQ0])],"isStart":false}),makeQuery(id+"F21.opExtrude","CAP_FACE",FACE,{"disambiguationData":[OSD([subQ0,sQuery(id+"F0.wireOp",EDGE,"E26.top"),sQuery(id+"F0.wireOp",EDGE,"E26.left"),sQuery(id+"F0.wireOp",EDGE,"E26.right")])],"isStart":false})],"blendedInto":[makeQuery(id+"F21.opExtrude","CAP_FACE",FACE,{"disambiguationData":[OSD([subQ0,sQuery(id+"F0.wireOp",EDGE,"E26.top"),sQuery(id+"F0.wireOp",EDGE,"E26.left"),sQuery(id+"F0.wireOp",EDGE,"E26.right")])],"isStart":false})]});}
            var Q1;
            {var subQ0=sQuery(id+"F0.wireOp",EDGE,"E25.bottom");Q1=makeQuery(id+"F22.opChamfer","BLEND_EDGE",EDGE,{"blendedFrom":[makeQuery(id+"F21.opExtrude","CAP_EDGE",EDGE,{"disambiguationData":[OSD([subQ0])],"isStart":false}),makeQuery(id+"F21.opExtrude","CAP_FACE",FACE,{"disambiguationData":[OSD([subQ0,sQuery(id+"F0.wireOp",EDGE,"E25.top"),sQuery(id+"F0.wireOp",EDGE,"E25.left"),sQuery(id+"F0.wireOp",EDGE,"E25.right")])],"isStart":false})],"blendedInto":[makeQuery(id+"F21.opExtrude","CAP_FACE",FACE,{"disambiguationData":[OSD([subQ0,sQuery(id+"F0.wireOp",EDGE,"E25.top"),sQuery(id+"F0.wireOp",EDGE,"E25.left"),sQuery(id+"F0.wireOp",EDGE,"E25.right")])],"isStart":false})]});}
            var Q2;
            {var subQ0=sQuery(id+"F0.wireOp",EDGE,"E24.top");Q2=makeQuery(id+"F22.opChamfer","BLEND_EDGE",EDGE,{"blendedFrom":[makeQuery(id+"F21.opExtrude","CAP_EDGE",EDGE,{"disambiguationData":[OSD([subQ0])],"isStart":false}),makeQuery(id+"F21.opExtrude","CAP_FACE",FACE,{"disambiguationData":[OSD([sQuery(id+"F0.wireOp",EDGE,"E24.bottom"),subQ0,sQuery(id+"F0.wireOp",EDGE,"E24.left"),sQuery(id+"F0.wireOp",EDGE,"E24.right")])],"isStart":false})],"blendedInto":[makeQuery(id+"F21.opExtrude","CAP_FACE",FACE,{"disambiguationData":[OSD([sQuery(id+"F0.wireOp",EDGE,"E24.bottom"),subQ0,sQuery(id+"F0.wireOp",EDGE,"E24.left"),sQuery(id+"F0.wireOp",EDGE,"E24.right")])],"isStart":false})]});}
            fillet(context, id + "F24", {"entities" : qUnion([Q0, Q1, Q2]), "radius" : 41.1 * mm, "tangentPropagation" : true, "allowEdgeOverflow" : false});
        }
        {
            var Q0;
            Q0=makeQuery(id+"F0.imprint","IMPRINT",FACE,{"disambiguationData":[TD([[makeQuery(id+"F0.imprint","IMPRINT",EDGE,{"derivedFrom":sQuery(id+"F0.wireOp",EDGE,"E27.bottom")}),-1.0]])]});
            extrude(context, id + "F25", {"entities" : qUnion([Q0]), "depth" : 3.17 * mm, "offsetDistance" : 25.4 * mm});
        }
        {
            var Q0;
            Q0=makeQuery(id+"F0.imprint","IMPRINT",FACE,{"disambiguationData":[TD([[makeQuery(id+"F0.imprint","IMPRINT",EDGE,{"derivedFrom":sQuery(id+"F0.wireOp",EDGE,"E30.bottom")}),-1.0]])]});
            extrude(context, id + "F26", {"entities" : qUnion([Q0]), "depth" : 25.4 * mm, "offsetDistance" : 25.4 * mm});
        }
        {
            var Q0;
            Q0=makeQuery(id+"F21.opExtrude","CAP_EDGE",EDGE,{"disambiguationData":[OSD([sQuery(id+"F0.wireOp",EDGE,"E25.bottom")])],"isStart":true});
            var Q1;
            Q1=makeQuery(id+"F21.opExtrude","CAP_EDGE",EDGE,{"disambiguationData":[OSD([sQuery(id+"F0.wireOp",EDGE,"E26.bottom")])],"isStart":true});
            var Q2;
            Q2=makeQuery(id+"F21.opExtrude","CAP_EDGE",EDGE,{"disambiguationData":[OSD([sQuery(id+"F0.wireOp",EDGE,"E24.top")])],"isStart":true});
            fillet(context, id + "F27", {"entities" : qUnion([Q0, Q1, Q2]), "radius" : 6.35 * mm, "tangentPropagation" : true, "allowEdgeOverflow" : false});
        }
        {
            var Q0;
            Q0=makeQuery(id+"F0.imprint","IMPRINT",FACE,{"disambiguationData":[TD([[makeQuery(id+"F0.imprint","IMPRINT",EDGE,{"derivedFrom":sQuery(id+"F0.wireOp",EDGE,"E31.bottom")}),-1.0]])]});
            extrude(context, id + "F28", {"entities" : qUnion([Q0]), "depth" : 3.17 * mm, "offsetDistance" : 25.4 * mm});
        }
        {
            var Q0;
            Q0=makeQuery(id+"F0.imprint","IMPRINT",FACE,{"disambiguationData":[TD([[makeQuery(id+"F0.imprint","IMPRINT",EDGE,{"derivedFrom":sQuery(id+"F0.wireOp",EDGE,"E33.bottom")}),1.0]])]});
            extrude(context, id + "F29", {"entities" : qUnion([Q0]), "depth" : 50.8 * mm, "offsetDistance" : 25.4 * mm});
        }
        {
            var Q0;
            {var subQ0=sQuery(id+"F0.wireOp",EDGE,"E32.bottom");Q0=makeQuery(id+"F0.imprint","IMPRINT",FACE,{"disambiguationData":[TD([[makeQuery(id+"F0.imprint","IMPRINT",EDGE,{"derivedFrom":subQ0}),1.0]])]});}
            extrude(context, id + "F30", {"entities" : qUnion([Q0]), "depth" : 25.4 * mm, "offsetDistance" : 25.4 * mm});
        }
        {
            var Q0;
            Q0=makeQuery(id+"F30.opExtrude","CAP_EDGE",EDGE,{"disambiguationData":[OSD([sQuery(id+"F0.wireOp",EDGE,"E32.bottom")])],"isStart":false});
            var Q1;
            Q1=makeQuery(id+"F30.opExtrude","CAP_EDGE",EDGE,{"disambiguationData":[OSD([sQuery(id+"F0.wireOp",EDGE,"E35")])],"isStart":false});
            fillet(context, id + "F31", {"entities" : qUnion([Q0, Q1]), "radius" : 127 * mm, "tangentPropagation" : true, "allowEdgeOverflow" : false});
        }
        {
            var Q0;
            {var subQ0=sQuery(id+"F0.wireOp",EDGE,"E32.bottom");Q0=makeQuery(id+"F0.imprint","IMPRINT",FACE,{"disambiguationData":[TD([[makeQuery(id+"F0.imprint","IMPRINT",EDGE,{"derivedFrom":subQ0}),1.0]])]});}
            var Q1;
            {var subQ0=sQuery(id+"F0.wireOp",EDGE,"E32.top");Q1=makeQuery(id+"F0.imprint","IMPRINT",FACE,{"disambiguationData":[TD([[makeQuery(id+"F0.imprint","IMPRINT",EDGE,{"derivedFrom":subQ0}),-1.0]])]});}
            extrude(context, id + "F32", {"entities" : qUnion([Q0, Q1]), "operationType" : NewBodyOperationType.ADD, "oppositeDirection" : true, "depth" : 3.17 * mm, "offsetDistance" : 25.4 * mm});
        }
        {
            var Q0;
            {var subQ0=sQuery(id+"F0.wireOp",EDGE,"E34.bottom");Q0=makeQuery(id+"F0.imprint","IMPRINT",FACE,{"disambiguationData":[TD([[makeQuery(id+"F0.imprint","IMPRINT",EDGE,{"derivedFrom":subQ0}),1.0]])]});}
            extrude(context, id + "F33", {"entities" : qUnion([Q0]), "depth" : 25.4 * mm, "offsetDistance" : 25.4 * mm});
        }
        {
            var Q0;
            Q0=makeQuery(id+"F33.opExtrude","CAP_EDGE",EDGE,{"disambiguationData":[OSD([sQuery(id+"F0.wireOp",EDGE,"E36")])],"isStart":false});
            var Q1;
            Q1=makeQuery(id+"F33.opExtrude","CAP_EDGE",EDGE,{"disambiguationData":[OSD([sQuery(id+"F0.wireOp",EDGE,"E34.bottom")])],"isStart":false});
            fillet(context, id + "F34", {"entities" : qUnion([Q0, Q1]), "radius" : 127 * mm, "tangentPropagation" : true, "allowEdgeOverflow" : false});
        }
        {
            var Q0;
            {var subQ0=sQuery(id+"F0.wireOp",EDGE,"E34.bottom");Q0=makeQuery(id+"F0.imprint","IMPRINT",FACE,{"disambiguationData":[TD([[makeQuery(id+"F0.imprint","IMPRINT",EDGE,{"derivedFrom":subQ0}),1.0]])]});}
            var Q1;
            {var subQ0=sQuery(id+"F0.wireOp",EDGE,"E34.top");Q1=makeQuery(id+"F0.imprint","IMPRINT",FACE,{"disambiguationData":[TD([[makeQuery(id+"F0.imprint","IMPRINT",EDGE,{"derivedFrom":subQ0}),-1.0]])]});}
            extrude(context, id + "F35", {"entities" : qUnion([Q0, Q1]), "operationType" : NewBodyOperationType.ADD, "oppositeDirection" : true, "depth" : 3.17 * mm, "offsetDistance" : 25.4 * mm});
        }
        {
            var Q0;
            Q0=makeQuery(id+"F0.imprint","IMPRINT",FACE,{"disambiguationData":[TD([[makeQuery(id+"F0.imprint","IMPRINT",EDGE,{"derivedFrom":sQuery(id+"F0.wireOp",EDGE,"E39.bottom")}),1.0]])]});
            extrude(context, id + "F36", {"entities" : qUnion([Q0]), "depth" : 25.4 * mm, "offsetDistance" : 25.4 * mm});
        }
        {
            var Q0;
            Q0=makeQuery(id+"F36.opExtrude","CAP_EDGE",EDGE,{"disambiguationData":[OSD([sQuery(id+"F0.wireOp",EDGE,"E39.top")])],"isStart":false});
            fillet(context, id + "F37", {"entities" : qUnion([Q0]), "radius" : 127 * mm, "tangentPropagation" : true, "allowEdgeOverflow" : false});
        }
        {
            var Q0;
            Q0=makeQuery(id+"F0.imprint","IMPRINT",FACE,{"disambiguationData":[TD([[makeQuery(id+"F0.imprint","IMPRINT",EDGE,{"derivedFrom":sQuery(id+"F0.wireOp",EDGE,"E39.bottom")}),1.0]])]});
            extrude(context, id + "F38", {"entities" : qUnion([Q0]), "operationType" : NewBodyOperationType.ADD, "oppositeDirection" : true, "depth" : 3.17 * mm, "offsetDistance" : 25.4 * mm});
        }
        {
            var Q0;
            {var subQ0=sQuery(id+"F0.wireOp",EDGE,"E32.top");Q0=makeQuery(id+"F0.imprint","IMPRINT",FACE,{"disambiguationData":[TD([[makeQuery(id+"F0.imprint","IMPRINT",EDGE,{"derivedFrom":subQ0}),-1.0]])]});}
            var Q1;
            {var subQ0=sQuery(id+"F0.wireOp",EDGE,"E6.bottom");Q1=makeQuery(id+"F0.imprint","IMPRINT",FACE,{"disambiguationData":[TD([[makeQuery(id+"F0.imprint","IMPRINT",EDGE,{"derivedFrom":subQ0}),-1.0]])]});}
            var Q2;
            Q2=makeQuery(id+"F0.imprint","IMPRINT",FACE,{"disambiguationData":[TD([[makeQuery(id+"F0.imprint","IMPRINT",EDGE,{"derivedFrom":sQuery(id+"F0.wireOp",EDGE,"E22.bottom")}),-1.0]])]});
            var Q3;
            Q3=makeQuery(id+"F0.imprint","IMPRINT",FACE,{"disambiguationData":[TD([[makeQuery(id+"F0.imprint","IMPRINT",EDGE,{"derivedFrom":sQuery(id+"F0.wireOp",EDGE,"E17.bottom")}),-1.0]])]});
            var Q4;
            Q4=makeQuery(id+"F0.imprint","IMPRINT",FACE,{"disambiguationData":[TD([[makeQuery(id+"F0.imprint","IMPRINT",EDGE,{"derivedFrom":sQuery(id+"F0.wireOp",EDGE,"E27.bottom")}),-1.0]])]});
            var Q5;
            Q5=makeQuery(id+"F0.imprint","IMPRINT",FACE,{"disambiguationData":[TD([[makeQuery(id+"F0.imprint","IMPRINT",EDGE,{"derivedFrom":sQuery(id+"F0.wireOp",EDGE,"E33.bottom")}),1.0]])]});
            var Q6;
            Q6=makeQuery(id+"F0.imprint","IMPRINT",FACE,{"disambiguationData":[TD([[makeQuery(id+"F0.imprint","IMPRINT",EDGE,{"derivedFrom":sQuery(id+"F0.wireOp",EDGE,"E41.bottom")}),-1.0]])]});
            var Q7;
            Q7=makeQuery(id+"F0.imprint","IMPRINT",FACE,{"disambiguationData":[TD([[makeQuery(id+"F0.imprint","IMPRINT",EDGE,{"derivedFrom":sQuery(id+"F0.wireOp",EDGE,"E25.bottom")}),1.0]])]});
            var Q8;
            {var subQ0=sQuery(id+"F0.wireOp",EDGE,"E34.top");Q8=makeQuery(id+"F0.imprint","IMPRINT",FACE,{"disambiguationData":[TD([[makeQuery(id+"F0.imprint","IMPRINT",EDGE,{"derivedFrom":subQ0}),-1.0]])]});}
            var Q9;
            {var subQ0=sQuery(id+"F0.wireOp",EDGE,"E32.bottom");Q9=makeQuery(id+"F0.imprint","IMPRINT",FACE,{"disambiguationData":[TD([[makeQuery(id+"F0.imprint","IMPRINT",EDGE,{"derivedFrom":subQ0}),1.0]])]});}
            var Q10;
            Q10=makeQuery(id+"F0.imprint","IMPRINT",FACE,{"disambiguationData":[TD([[makeQuery(id+"F0.imprint","IMPRINT",EDGE,{"derivedFrom":sQuery(id+"F0.wireOp",EDGE,"E38.bottom")}),1.0]])]});
            var Q11;
            Q11=makeQuery(id+"F0.imprint","IMPRINT",FACE,{"disambiguationData":[TD([[makeQuery(id+"F0.imprint","IMPRINT",EDGE,{"derivedFrom":sQuery(id+"F0.wireOp",EDGE,"E23.bottom")}),-1.0]])]});
            var Q12;
            {var subQ0=sQuery(id+"F0.wireOp",EDGE,"E4.bottom");Q12=makeQuery(id+"F0.imprint","IMPRINT",FACE,{"disambiguationData":[TD([[makeQuery(id+"F0.imprint","IMPRINT",EDGE,{"derivedFrom":subQ0}),-1.0]])]});}
            var Q13;
            {var subQ0=sQuery(id+"F0.wireOp",EDGE,"E12.top");Q13=makeQuery(id+"F0.imprint","IMPRINT",FACE,{"disambiguationData":[TD([[makeQuery(id+"F0.imprint","IMPRINT",EDGE,{"derivedFrom":subQ0}),1.0]])]});}
            var Q14;
            {var subQ0=sQuery(id+"F0.wireOp",EDGE,"E4.top");Q14=makeQuery(id+"F0.imprint","IMPRINT",FACE,{"disambiguationData":[TD([[makeQuery(id+"F0.imprint","IMPRINT",EDGE,{"derivedFrom":subQ0}),1.0]])]});}
            var Q15;
            Q15=makeQuery(id+"F0.imprint","IMPRINT",FACE,{"disambiguationData":[TD([[makeQuery(id+"F0.imprint","IMPRINT",EDGE,{"derivedFrom":sQuery(id+"F0.wireOp",EDGE,"E39.bottom")}),1.0]])]});
            var Q16;
            {var subQ0=sQuery(id+"F0.wireOp",EDGE,"E7.bottom");Q16=makeQuery(id+"F0.imprint","IMPRINT",FACE,{"disambiguationData":[TD([[makeQuery(id+"F0.imprint","IMPRINT",EDGE,{"derivedFrom":subQ0}),-1.0]])]});}
            var Q17;
            {var subQ3=sQuery(id+"F0.wireOp",EDGE,"E15");Q17=makeQuery(id+"F0.imprint","IMPRINT",FACE,{"disambiguationData":[TD([[makeQuery(id+"F0.imprint","IMPRINT",EDGE,{"derivedFrom":subQ3}),-1.0]])]});}
            var Q18;
            Q18=makeQuery(id+"F0.imprint","IMPRINT",FACE,{"disambiguationData":[TD([[makeQuery(id+"F0.imprint","IMPRINT",EDGE,{"derivedFrom":sQuery(id+"F0.wireOp",EDGE,"E30.bottom")}),-1.0]])]});
            var Q19;
            Q19=makeQuery(id+"F0.imprint","IMPRINT",FACE,{"disambiguationData":[TD([[makeQuery(id+"F0.imprint","IMPRINT",EDGE,{"derivedFrom":sQuery(id+"F0.wireOp",EDGE,"E20.top")}),-1.0]])]});
            var Q20;
            {var subQ0=sQuery(id+"F0.wireOp",EDGE,"E34.bottom");Q20=makeQuery(id+"F0.imprint","IMPRINT",FACE,{"disambiguationData":[TD([[makeQuery(id+"F0.imprint","IMPRINT",EDGE,{"derivedFrom":subQ0}),1.0]])]});}
            var Q21;
            Q21=makeQuery(id+"F0.imprint","IMPRINT",FACE,{"disambiguationData":[TD([[makeQuery(id+"F0.imprint","IMPRINT",EDGE,{"derivedFrom":sQuery(id+"F0.wireOp",EDGE,"E21.bottom")}),-1.0]])]});
            var Q22;
            Q22=makeQuery(id+"F0.imprint","IMPRINT",FACE,{"disambiguationData":[TD([[makeQuery(id+"F0.imprint","IMPRINT",EDGE,{"derivedFrom":sQuery(id+"F0.wireOp",EDGE,"E19.top")}),1.0]])]});
            var Q23;
            Q23=makeQuery(id+"F0.imprint","IMPRINT",FACE,{"disambiguationData":[TD([[makeQuery(id+"F0.imprint","IMPRINT",EDGE,{"derivedFrom":sQuery(id+"F0.wireOp",EDGE,"E24.bottom")}),-1.0]])]});
            var Q24;
            Q24=makeQuery(id+"F0.imprint","IMPRINT",FACE,{"disambiguationData":[TD([[makeQuery(id+"F0.imprint","IMPRINT",EDGE,{"derivedFrom":sQuery(id+"F0.wireOp",EDGE,"E18.top")}),1.0]])]});
            var Q25;
            {var subQ0=sQuery(id+"F0.wireOp",EDGE,"E12.bottom");Q25=makeQuery(id+"F0.imprint","IMPRINT",FACE,{"disambiguationData":[TD([[makeQuery(id+"F0.imprint","IMPRINT",EDGE,{"derivedFrom":subQ0}),-1.0]])]});}
            var Q26;
            {var subQ0=sQuery(id+"F0.wireOp",EDGE,"E7.top");Q26=makeQuery(id+"F0.imprint","IMPRINT",FACE,{"disambiguationData":[TD([[makeQuery(id+"F0.imprint","IMPRINT",EDGE,{"derivedFrom":subQ0}),1.0]])]});}
            var Q27;
            Q27=makeQuery(id+"F0.imprint","IMPRINT",FACE,{"disambiguationData":[TD([[makeQuery(id+"F0.imprint","IMPRINT",EDGE,{"derivedFrom":sQuery(id+"F0.wireOp",EDGE,"E26.bottom")}),1.0]])]});
            var Q28;
            {var subQ0=sQuery(id+"F0.wireOp",EDGE,"E16");Q28=makeQuery(id+"F0.imprint","IMPRINT",FACE,{"disambiguationData":[TD([[makeQuery(id+"F0.imprint","IMPRINT",EDGE,{"derivedFrom":subQ0}),-1.0]])]});}
            var Q29;
            Q29=makeQuery(id+"F0.imprint","IMPRINT",FACE,{"disambiguationData":[TD([[makeQuery(id+"F0.imprint","IMPRINT",EDGE,{"derivedFrom":sQuery(id+"F0.wireOp",EDGE,"E31.bottom")}),-1.0]])]});
            var Q30;
            {var subQ1=sQuery(id+"F0.wireOp",EDGE,"E14.top");Q30=makeQuery(id+"F0.imprint","IMPRINT",FACE,{"disambiguationData":[TD([[makeQuery(id+"F0.imprint","IMPRINT",EDGE,{"derivedFrom":subQ1}),1.0]])]});}
            var Q31;
            Q31=makeQuery(id+"F0.imprint","IMPRINT",FACE,{"disambiguationData":[TD([[makeQuery(id+"F0.imprint","IMPRINT",EDGE,{"derivedFrom":sQuery(id+"F0.wireOp",EDGE,"E0.bottom")}),-1.0]])]});
            var Q32;
            {var subQ0=sQuery(id+"F0.wireOp",EDGE,"E6.top");Q32=makeQuery(id+"F0.imprint","IMPRINT",FACE,{"disambiguationData":[TD([[makeQuery(id+"F0.imprint","IMPRINT",EDGE,{"derivedFrom":subQ0}),1.0]])]});}
            var Q33;
            Q33=makeQuery(id+"F0.imprint","IMPRINT",FACE,{"disambiguationData":[TD([[makeQuery(id+"F0.imprint","IMPRINT",EDGE,{"derivedFrom":sQuery(id+"F0.wireOp",EDGE,"E10.bottom")}),-1.0]])]});
            var Q34;
            {var subQ0=sQuery(id+"F0.wireOp",EDGE,"E37.bottom");Q34=makeQuery(id+"F0.imprint","IMPRINT",FACE,{"disambiguationData":[TD([[makeQuery(id+"F0.imprint","IMPRINT",EDGE,{"derivedFrom":subQ0}),1.0]])]});}
            extrude(context, id + "F39", {"entities" : qUnion([Q0, Q1, Q2, Q3, Q4, Q5, Q6, Q7, Q8, Q9, Q10, Q11, Q12, Q13, Q14, Q15, Q16, Q17, Q18, Q19, Q20, Q21, Q22, Q23, Q24, Q25, Q26, Q27, Q28, Q29, Q30, Q31, Q32, Q33, Q34]), "depth" : 25.4 * mm, "offsetDistance" : 25.4 * mm});
        }
        {
            var Q0;
            Q0=makeQuery(id+"F39.opExtrude","CAP_EDGE",EDGE,{"disambiguationData":[OSD([sQuery(id+"F0.wireOp",EDGE,"E41.bottom")])],"isStart":false});
            var Q1;
            Q1=makeQuery(id+"F39.opExtrude","CAP_EDGE",EDGE,{"disambiguationData":[OSD([sQuery(id+"F0.wireOp",EDGE,"E40")])],"isStart":false});
            var Q2;
            Q2=makeQuery(id+"F39.opExtrude","CAP_EDGE",EDGE,{"disambiguationData":[OSD([sQuery(id+"F0.wireOp",EDGE,"E37.bottom")])],"isStart":false});
            fillet(context, id + "F40", {"entities" : qUnion([Q0, Q1, Q2]), "radius" : 127 * mm, "tangentPropagation" : true, "allowEdgeOverflow" : false});
        }
        {
            var Q0;
            {var subQ0=sQuery(id+"F0.wireOp",EDGE,"E37.top");Q0=makeQuery(id+"F0.imprint","IMPRINT",FACE,{"disambiguationData":[TD([[makeQuery(id+"F0.imprint","IMPRINT",EDGE,{"derivedFrom":subQ0}),-1.0]])]});}
            var Q1;
            {var subQ0=sQuery(id+"F0.wireOp",EDGE,"E37.bottom");Q1=makeQuery(id+"F0.imprint","IMPRINT",FACE,{"disambiguationData":[TD([[makeQuery(id+"F0.imprint","IMPRINT",EDGE,{"derivedFrom":subQ0}),1.0]])]});}
            extrude(context, id + "F41", {"entities" : qUnion([Q0, Q1]), "operationType" : NewBodyOperationType.ADD, "oppositeDirection" : true, "depth" : 3.17 * mm, "offsetDistance" : 25.4 * mm});
        }
        {
            var Q0;
            Q0=makeQuery(id+"F0.imprint","IMPRINT",FACE,{"disambiguationData":[TD([[makeQuery(id+"F0.imprint","IMPRINT",EDGE,{"derivedFrom":sQuery(id+"F0.wireOp",EDGE,"E41.bottom")}),-1.0]])]});
            extrude(context, id + "F42", {"entities" : qUnion([Q0]), "operationType" : NewBodyOperationType.ADD, "oppositeDirection" : true, "depth" : 3.17 * mm, "offsetDistance" : 25.4 * mm});
        }
        {
            var Q0;
            {var subQ0=sQuery(id+"F0.wireOp",EDGE,"E42.bottom");Q0=makeQuery(id+"F0.imprint","IMPRINT",FACE,{"disambiguationData":[TD([[makeQuery(id+"F0.imprint","IMPRINT",EDGE,{"derivedFrom":subQ0}),-1.0]])]});}
            extrude(context, id + "F43", {"entities" : qUnion([Q0]), "depth" : 25.4 * mm, "offsetDistance" : 25.4 * mm});
        }
        {
            var Q0;
            Q0=makeQuery(id+"F43.opExtrude","CAP_EDGE",EDGE,{"disambiguationData":[OSD([sQuery(id+"F0.wireOp",EDGE,"E42.bottom")])],"isStart":false});
            var Q1;
            Q1=makeQuery(id+"F43.opExtrude","CAP_EDGE",EDGE,{"disambiguationData":[OSD([sQuery(id+"F0.wireOp",EDGE,"E43")])],"isStart":false});
            fillet(context, id + "F44", {"entities" : qUnion([Q0, Q1]), "radius" : 127 * mm, "tangentPropagation" : true, "allowEdgeOverflow" : false});
        }
        {
            var Q0;
            {var subQ0=sQuery(id+"F0.wireOp",EDGE,"E42.top");Q0=makeQuery(id+"F0.imprint","IMPRINT",FACE,{"disambiguationData":[TD([[makeQuery(id+"F0.imprint","IMPRINT",EDGE,{"derivedFrom":subQ0}),1.0]])]});}
            var Q1;
            {var subQ0=sQuery(id+"F0.wireOp",EDGE,"E42.bottom");Q1=makeQuery(id+"F0.imprint","IMPRINT",FACE,{"disambiguationData":[TD([[makeQuery(id+"F0.imprint","IMPRINT",EDGE,{"derivedFrom":subQ0}),-1.0]])]});}
            extrude(context, id + "F45", {"entities" : qUnion([Q0, Q1]), "operationType" : NewBodyOperationType.ADD, "oppositeDirection" : true, "depth" : 3.17 * mm, "offsetDistance" : 25.4 * mm});
        }
    });
